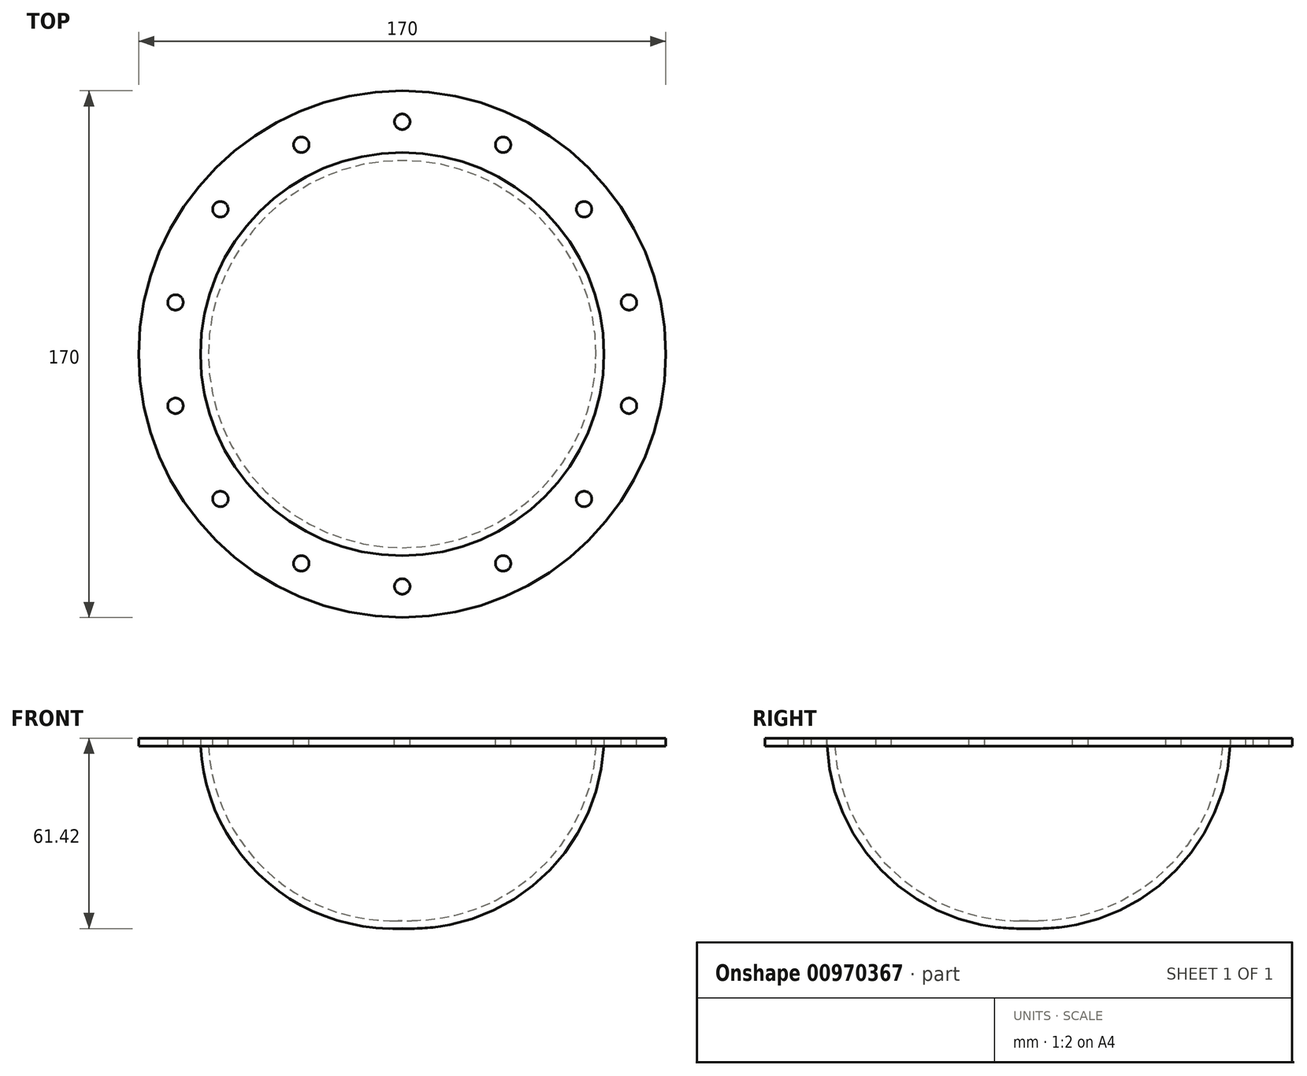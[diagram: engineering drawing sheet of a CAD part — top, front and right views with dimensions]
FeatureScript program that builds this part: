
annotation { "Feature Type Name" : "Feature", "Feature Type Description" : "" }
export const myFeature = defineFeature(function(context is Context, id is Id, definition is map)
    precondition{}
    {
        {
            var Q0;
            Q0=qCreatedBy(makeId("Right.planeOp"),FACE);
            var sketch = newSketch(context, id + "F0", { "sketchPlane" : qUnion([Q0])});
            skLineSegment(sketch, "E0", {"start": v(0, 0) * mm, "end": v(65, 0) * mm});
            skLineSegment(sketch, "E1", {"start": v(0, 0) * mm, "end": v(0, 65) * mm});
            skArc(sketch, "E2", {"start": v(65, 0) * mm, "mid": v(46.92, 46.92) * mm, "end": v(0, 65) * mm});
            skSolve(sketch);
        }
        {
            var Q0;
            Q0=makeQuery(id+"F0.imprint","IMPRINT",FACE,{"disambiguationData":[TD([[makeQuery(id+"F0.imprint","IMPRINT",EDGE,{"derivedFrom":sQuery(id+"F0.wireOp",EDGE,"E0")}),1.0]])]});
            var Q1;
            Q1=sQuery(id+"F0.wireOp",EDGE,"E1");
            revolve(context, id + "F1", {"surfaceOperationType" : NewSurfaceOperationType.NEW, "entities" : qUnion([Q0]), "axis" : qUnion([Q1]), "revolveType" : RevolveType.FULL});
        }
        {
            var Q0;
            Q0=makeQuery(id+"F1.opRevolve","SWEPT_FACE",FACE,{"disambiguationData":[OSD([sQuery(id+"F0.wireOp",EDGE,"E0")])]});
            shell(context, id + "F2", {"entities" : qUnion([Q0]), "thickness" : 2.5 * mm});
        }
        {
            var Q0;
            Q0=qCreatedBy(makeId("Top.planeOp"),FACE);
            var sketch = newSketch(context, id + "F3", { "sketchPlane" : qUnion([Q0])});
            skCircle(sketch, "E3", {"center": v(0, 0) * mm, "radius": 65 * mm});
            skCircle(sketch, "E4", {"center": v(0, 0) * mm, "radius": 85 * mm});
            skSolve(sketch);
        }
        {
            var Q0;
            Q0=makeQuery(id+"F3.imprint","IMPRINT",FACE,{"disambiguationData":[TD([[makeQuery(id+"F3.imprint","IMPRINT",EDGE,{"derivedFrom":sQuery(id+"F3.wireOp",EDGE,"E3")}),-1.0]])]});
            extrude(context, id + "F4", {"entities" : qUnion([Q0]), "operationType" : NewBodyOperationType.ADD, "depth" : 2.5 * mm, "offsetDistance" : 25 * mm});
        }
        {
            var Q0;
            Q0=makeQuery(id+"F4.opExtrude","CAP_FACE",FACE,{"disambiguationData":[OSD([sQuery(id+"F3.wireOp",EDGE,"E3"),sQuery(id+"F3.wireOp",EDGE,"E4")])],"isStart":false});
            var sketch = newSketch(context, id + "F5", { "sketchPlane" : qUnion([Q0])});
            skLineSegment(sketch, "E5", {"start": v(0, 0) * mm, "end": v(0, 75) * mm});
            skCircle(sketch, "E6", {"center": v(0, 75) * mm, "radius": 2.5 * mm});
            skCircle(sketch, "E7.1.0", {"center": v(-32.54, 67.57) * mm, "radius": 2.5 * mm});
            skCircle(sketch, "E7.2.0", {"center": v(-58.64, 46.76) * mm, "radius": 2.5 * mm});
            skCircle(sketch, "E7.3.0", {"center": v(-73.12, 16.69) * mm, "radius": 2.5 * mm});
            skCircle(sketch, "E7.4.0", {"center": v(-73.12, -16.69) * mm, "radius": 2.5 * mm});
            skCircle(sketch, "E7.5.0", {"center": v(-58.64, -46.76) * mm, "radius": 2.5 * mm});
            skCircle(sketch, "E7.6.0", {"center": v(-32.54, -67.57) * mm, "radius": 2.5 * mm});
            skCircle(sketch, "E7.7.0", {"center": v(0, -75) * mm, "radius": 2.5 * mm});
            skCircle(sketch, "E7.8.0", {"center": v(32.54, -67.57) * mm, "radius": 2.5 * mm});
            skCircle(sketch, "E7.9.0", {"center": v(58.64, -46.76) * mm, "radius": 2.5 * mm});
            skCircle(sketch, "E7.10.0", {"center": v(73.12, -16.69) * mm, "radius": 2.5 * mm});
            skCircle(sketch, "E7.11.0", {"center": v(73.12, 16.69) * mm, "radius": 2.5 * mm});
            skCircle(sketch, "E7.12.0", {"center": v(58.64, 46.76) * mm, "radius": 2.5 * mm});
            skCircle(sketch, "E7.13.0", {"center": v(32.54, 67.57) * mm, "radius": 2.5 * mm});
            skPoint(sketch, "E7.center", {"position": v(0, 0) * mm});
            skSolve(sketch);
        }
        {
            var Q0;
            Q0 = qSketchRegion(id + "F5", true);
            extrude(context, id + "F6", {"entities" : qUnion([Q0]), "operationType" : NewBodyOperationType.REMOVE, "oppositeDirection" : true, "depth" : 25 * mm, "offsetDistance" : 25 * mm});
        }
    });
